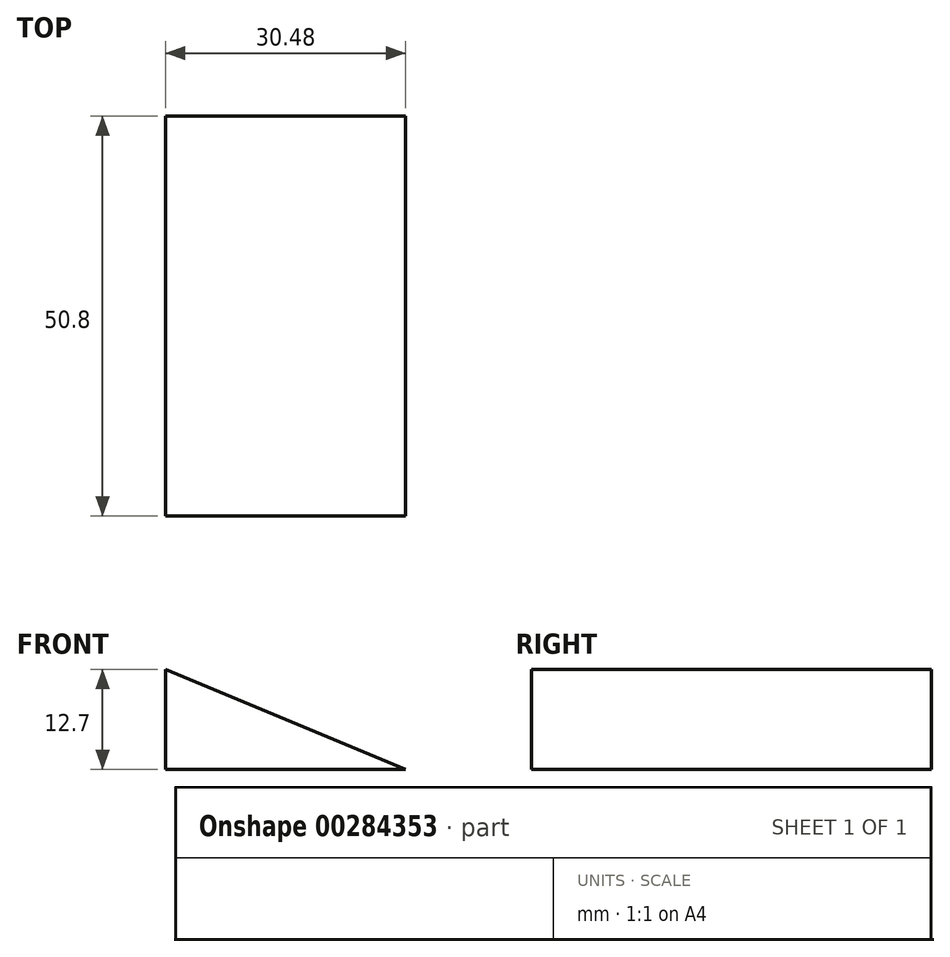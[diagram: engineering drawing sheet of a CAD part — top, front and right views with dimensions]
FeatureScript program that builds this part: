
annotation { "Feature Type Name" : "Feature", "Feature Type Description" : "" }
export const myFeature = defineFeature(function(context is Context, id is Id, definition is map)
    precondition{}
    {
        {
            var Q0;
            Q0=qCreatedBy(makeId("Front.planeOp"),FACE);
            var sketch = newSketch(context, id + "F0", { "sketchPlane" : qUnion([Q0])});
            skLineSegment(sketch, "E0", {"start": v(0, 0) * mm, "end": v(0, 12.7) * mm});
            skLineSegment(sketch, "E1", {"start": v(0, 0) * mm, "end": v(30.48, 0) * mm});
            skLineSegment(sketch, "E2", {"start": v(30.48, 0) * mm, "end": v(0, 12.7) * mm});
            skSolve(sketch);
        }
        {
            var Q0;
            Q0 = qSketchRegion(id + "F0", true);
            extrude(context, id + "F1", {"entities" : qUnion([Q0]), "depth" : 50.8 * mm});
        }
    });
